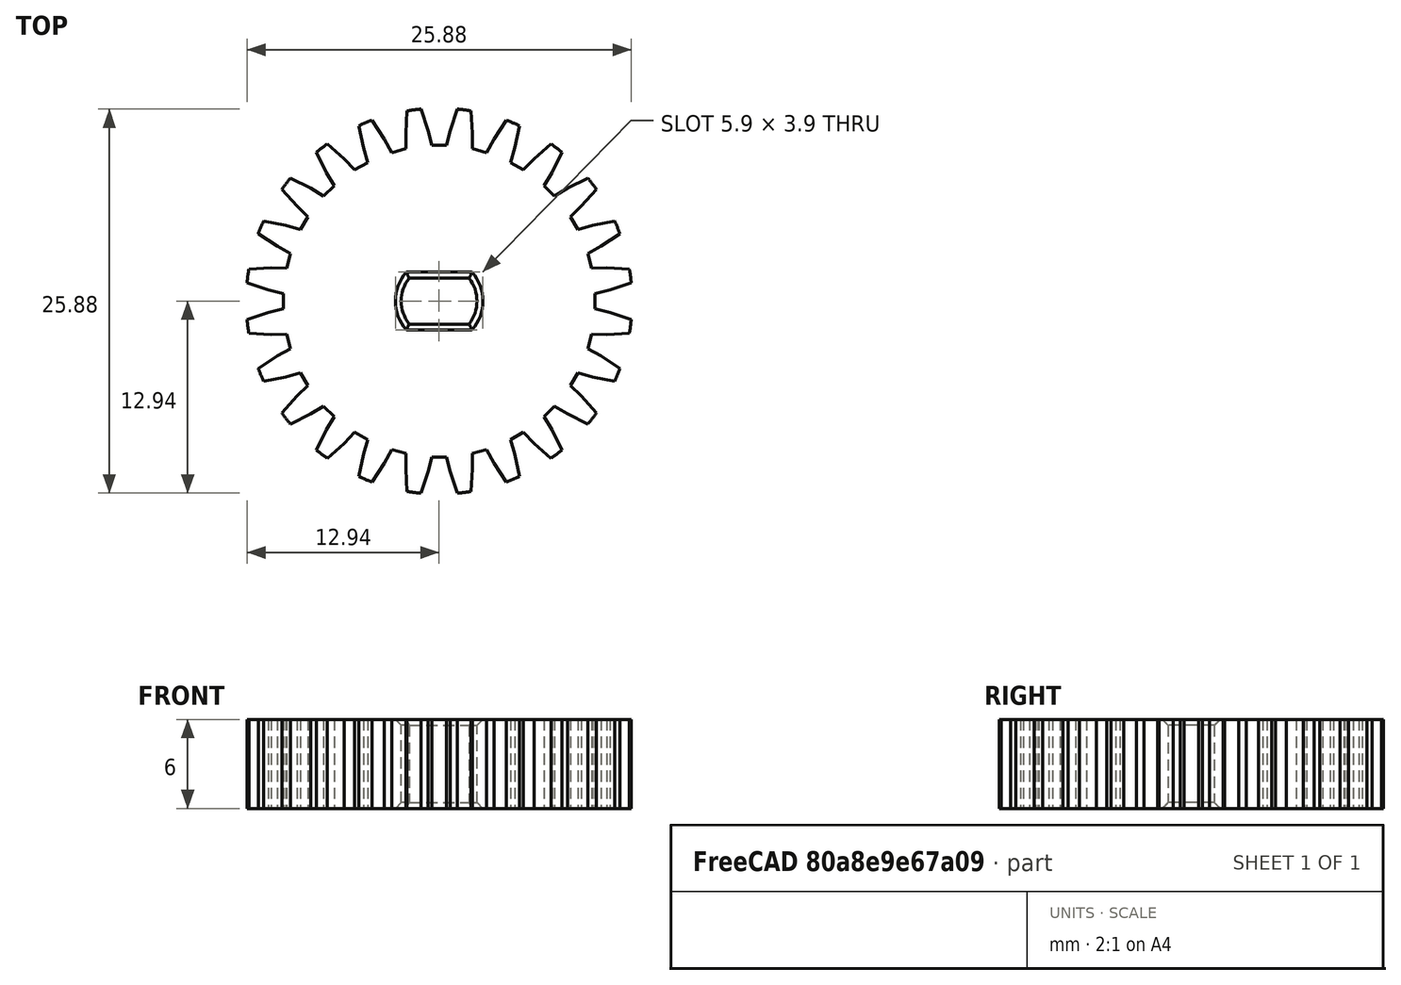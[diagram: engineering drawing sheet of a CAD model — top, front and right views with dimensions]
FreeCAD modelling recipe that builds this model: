
FCSTD DOCUMENT  (FreeCAD 0.18R4 (GitTag))
Label: Stepper_Motor_Gear
License: All rights reserved
LicenseURL: http://en.wikipedia.org/wiki/All_rights_reserved
objects: Sketcher::SketchObject×2, PartDesign::Pad×1, PartDesign::Pocket×1, PartDesign::PolarPattern×1, PartDesign::Chamfer×1, PartDesign::Body×1, Mesh::Feature×1
note: 9 computed .brp shape members not serialized (recipe doc carries the construction recipe); baked Part::Feature solids carry a one-line shape summary decoded from their .brp

FEATURE [Sketcher::SketchObject] Sketch
  MapMode = 5
  Support = -> [XY_Plane]
  sketch-geometry (6):
    g0: Circle CenterX=0 CenterY=0 CenterZ=0 NormalX=0 NormalY=0 NormalZ=1 AngleXU=0 Radius=13
    g1: LineSegment StartX=-2.02485 StartY=1.55 StartZ=0 EndX=2.02485 EndY=1.55 EndZ=0
    g2: LineSegment StartX=-2.02485 StartY=-1.55 StartZ=0 EndX=2.02485 EndY=-1.55 EndZ=0
    g3: LineSegment [constr] StartX=0 StartY=-4.81277 StartZ=0 EndX=0 EndY=4.82199 EndZ=0
    g4: ArcOfCircle CenterX=0 CenterY=0 CenterZ=0 NormalX=0 NormalY=0 NormalZ=1 AngleXU=0 Radius=2.55 StartAngle=2.48825 EndAngle=3.79493
    g5: ArcOfCircle CenterX=0 CenterY=0 CenterZ=0 NormalX=0 NormalY=0 NormalZ=1 AngleXU=0 Radius=2.55 StartAngle=5.62984 EndAngle=6.93653
  constraints (15):
    c: Radius(g0) = 13
    c: Parallel(g1,g2)
    c: Horizontal(g1)
    c: Equal(g1,g2)
    c: Coincident(g0,g-1)
    c: Symmetric(g1,g1,g3)
    c: PointOnObject(g0,g3)
    c: DistanceY(g0,g1) = 1.55
    c: Coincident(g4,g1)
    c: Coincident(g4,g2)
    c: Coincident(g4,g0)
    c: Radius(g4) = 2.55
    c: Coincident(g5,g1)
    c: Coincident(g5,g0)
    c: Coincident(g5,g2)
FEATURE [PartDesign::Pad] Pad
  Length = 6
  Length2 = 100
  Profile = -> Sketch
  Reversed = true
  Type = 0
FEATURE [Sketcher::SketchObject] Sketch001
  ExternalGeometry = -> [Pad]
  MapMode = 5
  Support = -> [Pad]
  sketch-geometry (9):
    g0: LineSegment [constr] StartX=0 StartY=0 StartZ=0 EndX=0 EndY=13 EndZ=0
    g1: LineSegment StartX=-0.5 StartY=10.5 StartZ=0 EndX=0.5 EndY=10.5 EndZ=0
    g2: LineSegment [constr] StartX=-0.75 StartY=11.5 StartZ=0 EndX=0.75 EndY=11.5 EndZ=0
    g3: LineSegment [constr] StartX=-1.25 StartY=13 StartZ=0 EndX=1.25 EndY=13 EndZ=0
    g4: LineSegment StartX=-0.5 StartY=10.5 StartZ=0 EndX=-0.75 EndY=11.5 EndZ=0
    g5: LineSegment StartX=-0.75 StartY=11.5 StartZ=0 EndX=-1.25 EndY=13 EndZ=0
    g6: LineSegment StartX=-1.25 StartY=13 StartZ=0 EndX=1.25 EndY=13 EndZ=0
    g7: LineSegment StartX=1.25 StartY=13 StartZ=0 EndX=0.75 EndY=11.5 EndZ=0
    g8: LineSegment StartX=0.75 StartY=11.5 StartZ=0 EndX=0.5 EndY=10.5 EndZ=0
  constraints (22):
    c: PointOnObject(g0,g-2)
    c: Coincident(g0,g-1)
    c: PointOnObject(g0,g-3)
    c: Symmetric(g1,g1,g0)
    c: DistanceY(g-1,g1) = 10.5
    c: DistanceX(g1,g1) = 1
    c: Symmetric(g2,g2,g0)
    c: DistanceY(g1,g2) = 1
    c: DistanceX(g2,g2) = 1.5
    c: Symmetric(g3,g3,g0)
    c: PointOnObject(g0,g3)
    c: DistanceX(g3,g3) = 2.5
    c: Coincident(g4,g1)
    c: Coincident(g4,g5)
    c: Coincident(g4,g2)
    c: Coincident(g6,g5)
    c: Coincident(g6,g3)
    c: Coincident(g6,g3)
    c: Coincident(g6,g7)
    c: Coincident(g7,g2)
    c: Coincident(g7,g8)
    c: Coincident(g8,g1)
FEATURE [PartDesign::Pocket] Pocket
  BaseFeature = -> Pad
  Length = 6
  Length2 = 100
  Profile = -> Sketch001
  Type = 0
FEATURE [PartDesign::PolarPattern] PolarPattern
  Angle = 360
  Axis = -> Sketch001 [N_Axis]
  BaseFeature = -> Pocket
  Occurrences = 24
  Originals = -> [Pocket]
FEATURE [PartDesign::Chamfer] Chamfer
  Base = -> PolarPattern [Edge149,Edge148,Edge150,Edge298,Edge299,Edge151,Edge297,Edge296]
  BaseFeature = -> PolarPattern
  Size = 0.4
FEATURE [PartDesign::Body] Body
  Group = -> [Sketch,Pad,Sketch001,Pocket,PolarPattern,Chamfer]
  Origin = -> Origin
  Tip = -> Chamfer
FEATURE [Mesh::Feature] Mesh  label="Chamfer (Meshed)"
